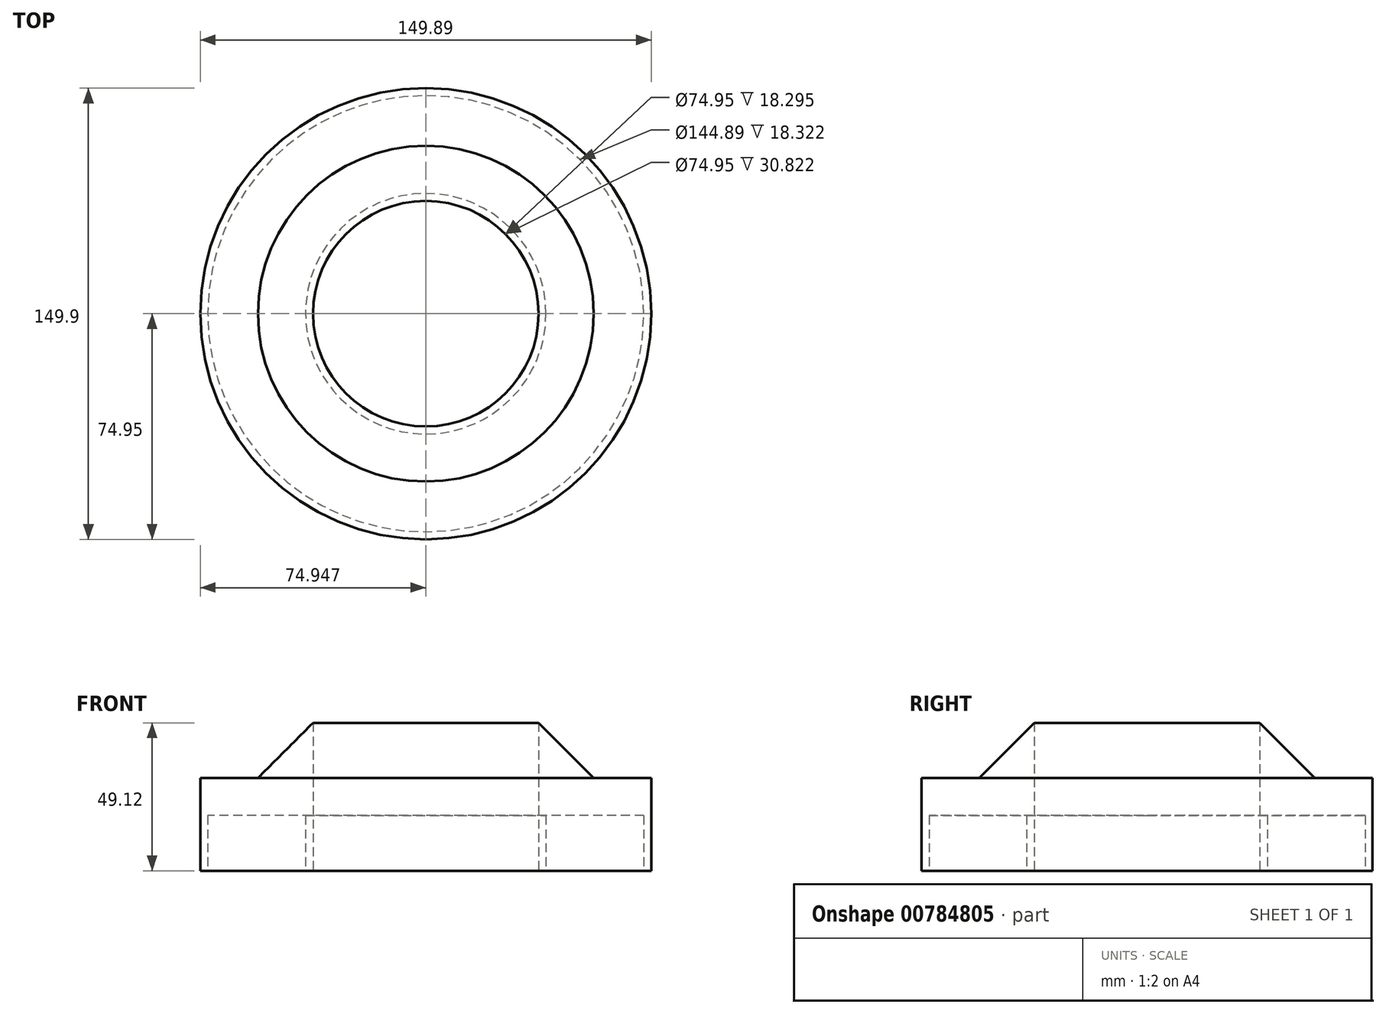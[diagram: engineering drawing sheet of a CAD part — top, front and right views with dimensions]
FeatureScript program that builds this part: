
annotation { "Feature Type Name" : "Feature", "Feature Type Description" : "" }
export const myFeature = defineFeature(function(context is Context, id is Id, definition is map)
    precondition{}
    {
        {
            var Q0;
            Q0=qCreatedBy(makeId("Front.planeOp"),FACE);
            var sketch = newSketch(context, id + "F0", { "sketchPlane" : qUnion([Q0])});
            skLineSegment(sketch, "E0.bottom", {"start": v(37.47, -30.82) * mm, "end": v(-37.47, -30.82) * mm});
            skLineSegment(sketch, "E0.top", {"start": v(37.47, 30.82) * mm, "end": v(-37.47, 30.82) * mm});
            skLineSegment(sketch, "E0.left", {"start": v(37.47, -30.82) * mm, "end": v(37.47, 30.82) * mm});
            skLineSegment(sketch, "E0.right", {"start": v(-37.47, -30.82) * mm, "end": v(-37.47, 30.82) * mm});
            skPoint(sketch, "E0.middle", {"position": v(0, 0) * mm});
            skLineSegment(sketch, "E1.bottom", {"start": v(37.47, 30.82) * mm, "end": v(0, 30.82) * mm});
            skLineSegment(sketch, "E1.top", {"start": v(37.47, 0) * mm, "end": v(0, 0) * mm});
            skLineSegment(sketch, "E1.left", {"start": v(37.47, 30.82) * mm, "end": v(37.47, 0) * mm});
            skLineSegment(sketch, "E1.right", {"start": v(0, 30.82) * mm, "end": v(0, 0) * mm});
            skLineSegment(sketch, "E2.bottom", {"start": v(-37.47, -30.82) * mm, "end": v(0, -30.82) * mm});
            skLineSegment(sketch, "E2.top", {"start": v(-37.47, 0) * mm, "end": v(0, 0) * mm});
            skLineSegment(sketch, "E2.left", {"start": v(-37.47, -30.82) * mm, "end": v(-37.47, 0) * mm});
            skLineSegment(sketch, "E2.right", {"start": v(0, -30.82) * mm, "end": v(0, 0) * mm});
            skSolve(sketch);
        }
        {
            var Q0;
            {var subQ4=sQuery(id+"F0.wireOp",EDGE,"E1.top");Q0=makeQuery(id+"F0.imprint","IMPRINT",FACE,{"disambiguationData":[TD([[makeQuery(id+"F0.imprint","IMPRINT",EDGE,{"derivedFrom":subQ4}),1.0]])]});}
            var sketch = newSketch(context, id + "F1", { "sketchPlane" : qUnion([Q0])});
            skLineSegment(sketch, "E3.bottom", {"start": v(37.47, 30.83) * mm, "end": v(27.02, 30.83) * mm});
            skLineSegment(sketch, "E3.top", {"start": v(37.47, 9.2) * mm, "end": v(27.02, 9.2) * mm});
            skLineSegment(sketch, "E3.left", {"start": v(37.47, 30.83) * mm, "end": v(37.47, 9.2) * mm});
            skLineSegment(sketch, "E3.right", {"start": v(27.02, 30.83) * mm, "end": v(27.02, 9.2) * mm});
            skSolve(sketch);
        }
        {
            var Q0;
            {var subQ4=sQuery(id+"F0.wireOp",EDGE,"E1.top");Q0=makeQuery(id+"F1.imprint","IMPRINT",FACE,{"disambiguationData":[TD([[makeQuery(id+"F1.imprint","IMPRINT",EDGE,{"derivedFrom":makeQuery(id+"F0.imprint","IMPRINT",EDGE,{"derivedFrom":subQ4})}),1.0]])]});}
            var Q1;
            {var subQ4=sQuery(id+"F0.wireOp",EDGE,"E1.top");Q1=makeQuery(id+"F0.imprint","IMPRINT",FACE,{"disambiguationData":[TD([[makeQuery(id+"F0.imprint","IMPRINT",EDGE,{"derivedFrom":subQ4}),-1.0]])]});}
            var Q2;
            Q2=sQuery(id+"F0.wireOp",EDGE,"E0.right");
            revolve(context, id + "F2", {"surfaceOperationType" : NewSurfaceOperationType.NEW, "entities" : qUnion([Q0, Q1]), "axis" : qUnion([Q2]), "revolveType" : RevolveType.FULL});
        }
        {
            var Q0;
            Q0=makeQuery(id+"F2.opRevolve","SWEPT_EDGE",EDGE,{"disambiguationData":[OSD([sQuery(id+"F0.wireOp",EDGE,"E0.top"),sQuery(id+"F0.wireOp",EDGE,"E0.left")])]});
            chamfer(context, id + "F3", {"entities" : qUnion([Q0]), "width" : 50 * mm, "tangentPropagation" : true});
        }
        {
            var Q0;
            Q0=makeQuery(id+"F2.opRevolve","SWEPT_FACE",FACE,{"disambiguationData":[OSD([sQuery(id+"F0.wireOp",EDGE,"E0.bottom")])]});
            shell(context, id + "F4", {"entities" : qUnion([Q0]), "thickness" : 2.5 * mm});
        }
        {
            var Q0;
            Q0=makeQuery(id+"F4.opShell","OFFSET_FACE",FACE,{"disambiguationData":[OSD([sQuery(id+"F0.wireOp",EDGE,"E1.top")])]});
            extrude(context, id + "F5", {"entities" : qUnion([Q0]), "operationType" : NewBodyOperationType.ADD, "depth" : 10 * mm, "offsetDistance" : 25 * mm});
        }
    });
